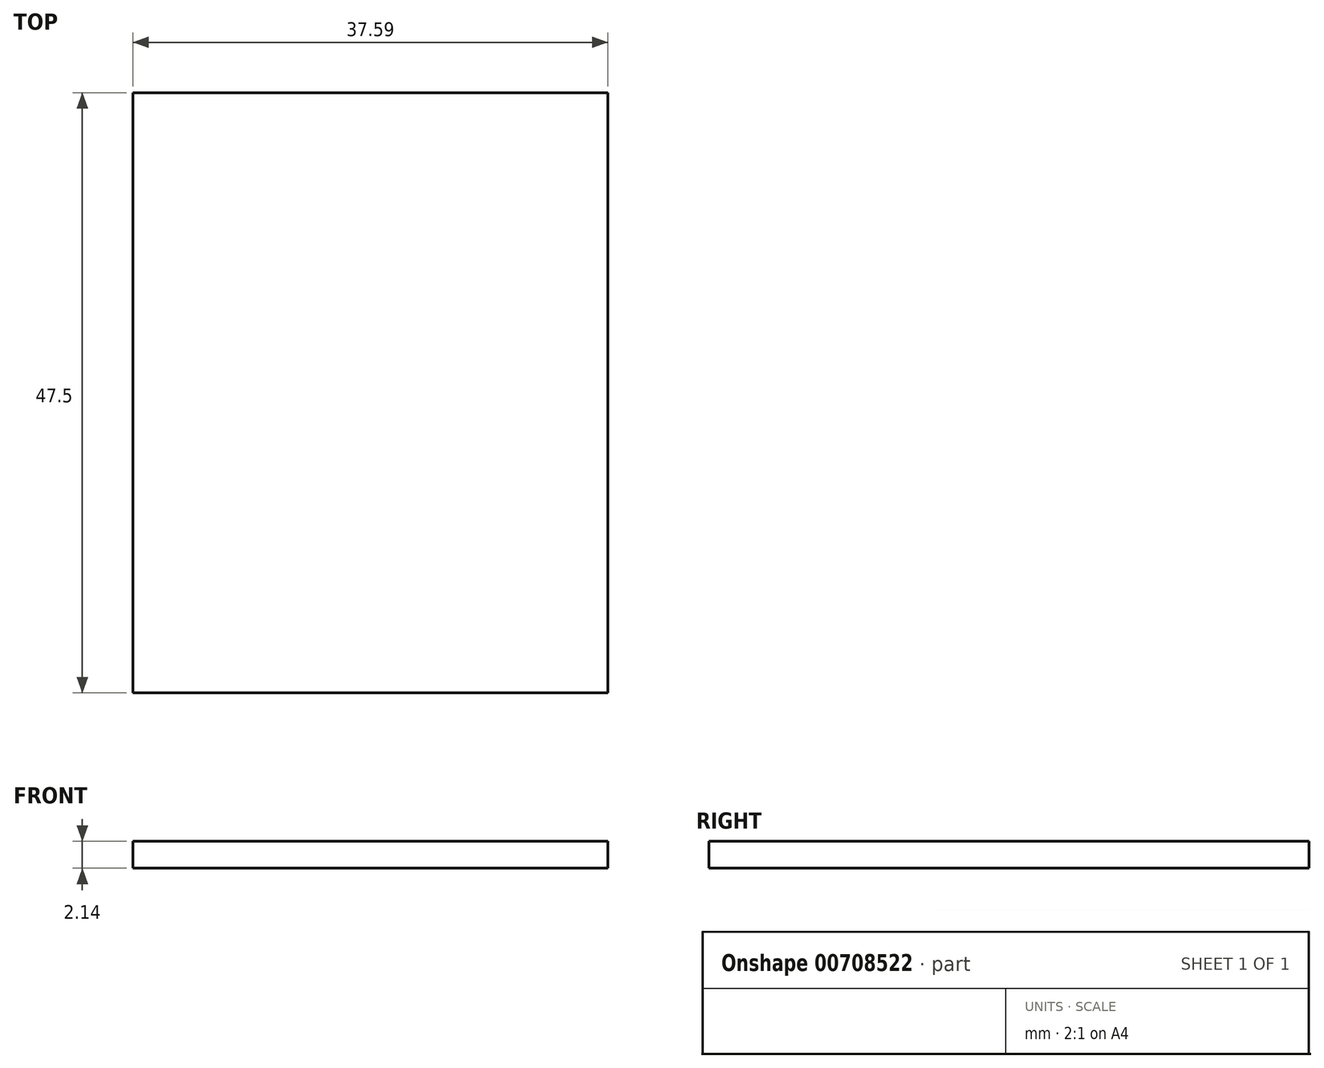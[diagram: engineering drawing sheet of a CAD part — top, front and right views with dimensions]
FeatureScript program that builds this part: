
annotation { "Feature Type Name" : "Feature", "Feature Type Description" : "" }
export const myFeature = defineFeature(function(context is Context, id is Id, definition is map)
    precondition{}
    {
        {
            var Q0;
            Q0=qCreatedBy(makeId("Front.planeOp"),FACE);
            var sketch = newSketch(context, id + "F0", { "sketchPlane" : qUnion([Q0])});
            skLineSegment(sketch, "E0.bottom", {"start": v(-55.44, 9) * mm, "end": v(-17.85, 9) * mm});
            skLineSegment(sketch, "E0.top", {"start": v(-55.44, 6.85) * mm, "end": v(-17.85, 6.85) * mm});
            skLineSegment(sketch, "E0.left", {"start": v(-55.44, 9) * mm, "end": v(-55.44, 6.85) * mm});
            skLineSegment(sketch, "E0.right", {"start": v(-17.85, 9) * mm, "end": v(-17.85, 6.85) * mm});
            skSolve(sketch);
        }
        {
            var Q0;
            Q0=makeQuery(id+"F0.imprint","IMPRINT",FACE,{"disambiguationData":[TD([[makeQuery(id+"F0.imprint","IMPRINT",EDGE,{"derivedFrom":sQuery(id+"F0.wireOp",EDGE,"E0.bottom")}),-1.0]])]});
            extrude(context, id + "F1", {"entities" : qUnion([Q0]), "depth" : 47.5 * mm, "offsetDistance" : 25.4 * mm});
        }
    });
